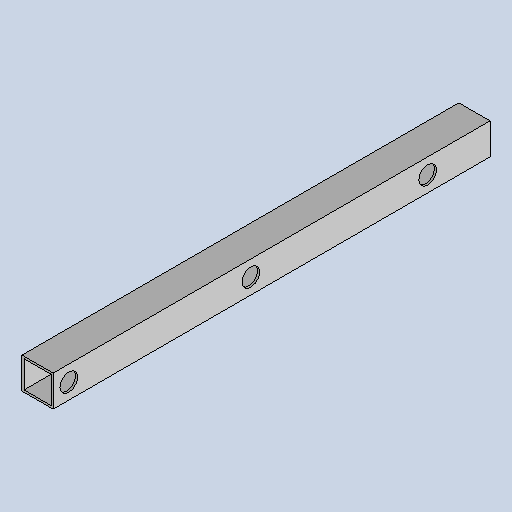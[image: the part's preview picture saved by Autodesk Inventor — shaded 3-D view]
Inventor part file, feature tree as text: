
AUTODESK INVENTOR PART (.ipt)
format: ipt  version: 2025.1 (Build 291241020, 241B)  size: 150,016 bytes
history: native  units: mm
features: extrude x2, sketch x2, projected_geometry x1
ambient origin geometry x8: Origin, YZ Plane, XZ Plane, XY Plane, X Axis, Y Axis, Z Axis, Center Point
bodies: Body1 (feature_tree)
feature tree (5):
  extrude  "Extrusion3"  Depth=30.0mm
  extrude  "Extrusion4"  Depth=2.0mm
  sketch  "Sketch9"  dims[d61=500.0mm d172=30.0mm]
  sketch  "Sketch10"  dims[d173=30.0mm d174=2.0mm d175=420.0mm d176=0.0mm d177=17.0mm d178=17.0mm d179=0.0mm d180=0.0mm d181=30.0mm d182=90.0mm d183=260.0mm d184=435.0mm d185=500.0mm d186=17.0mm]
  projected_geometry  "Projected Loop3"
